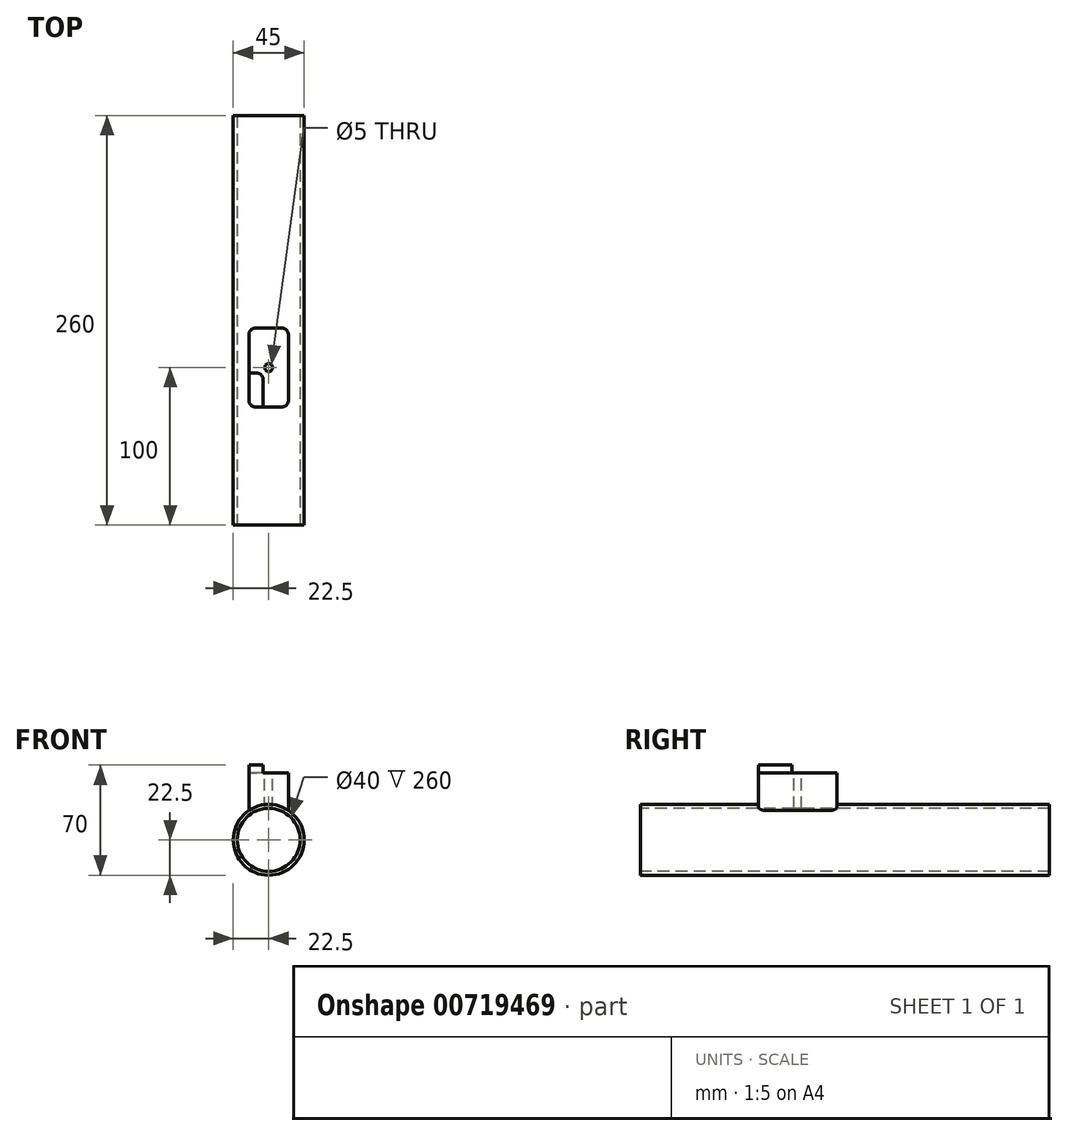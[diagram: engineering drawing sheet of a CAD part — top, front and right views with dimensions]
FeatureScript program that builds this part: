
annotation { "Feature Type Name" : "Feature", "Feature Type Description" : "" }
export const myFeature = defineFeature(function(context is Context, id is Id, definition is map)
    precondition{}
    {
        {
            var Q0;
            Q0=qCreatedBy(makeId("Right.planeOp"),FACE);
            var sketch = newSketch(context, id + "F0", { "sketchPlane" : qUnion([Q0])});
            skLineSegment(sketch, "E0", {"start": v(-15.87, 0) * mm, "end": v(20, 0) * mm, "construction": true});
            skLineSegment(sketch, "E1", {"start": v(-100, 22.5) * mm, "end": v(0, 22.5) * mm});
            skLineSegment(sketch, "E2", {"start": v(-100, 22.5) * mm, "end": v(-100, 20) * mm});
            skLineSegment(sketch, "E3", {"start": v(-100, 20) * mm, "end": v(0, 20) * mm});
            skLineSegment(sketch, "E4.MirrorCS", {"start": v(100, 20) * mm, "end": v(0, 20) * mm});
            skLineSegment(sketch, "E5.MirrorCS", {"start": v(100, 22.5) * mm, "end": v(0, 22.5) * mm});
            skLineSegment(sketch, "E6", {"start": v(-25, 22.5) * mm, "end": v(-25, 42.5) * mm});
            skLineSegment(sketch, "E7", {"start": v(-25, 42.5) * mm, "end": v(0, 42.5) * mm});
            skLineSegment(sketch, "E8", {"start": v(0, 42.5) * mm, "end": v(25, 42.5) * mm});
            skLineSegment(sketch, "E9", {"start": v(25, 42.5) * mm, "end": v(25, 22.5) * mm});
            skLineSegment(sketch, "E10", {"start": v(100, 22.5) * mm, "end": v(160, 22.5) * mm});
            skLineSegment(sketch, "E11", {"start": v(100, 20) * mm, "end": v(160, 20) * mm});
            skLineSegment(sketch, "E12", {"start": v(160, 20) * mm, "end": v(160, 22.5) * mm});
            skSolve(sketch);
        }
        {
            var Q0;
            {var subQ0=sQuery(id+"F0.wireOp",EDGE,"E2");Q0=makeQuery(id+"F0.imprint","IMPRINT",FACE,{"disambiguationData":[TD([[makeQuery(id+"F0.imprint","IMPRINT",EDGE,{"derivedFrom":subQ0}),1.0]])]});}
            var Q1;
            Q1=sQuery(id+"F0.wireOp",EDGE,"E0");
            revolve(context, id + "F1", {"surfaceOperationType" : NewSurfaceOperationType.NEW, "entities" : qUnion([Q0]), "axis" : qUnion([Q1]), "revolveType" : RevolveType.FULL});
        }
        {
            var Q0;
            {var subQ0=sQuery(id+"F0.wireOp",EDGE,"E6");Q0=makeQuery(id+"F0.imprint","IMPRINT",FACE,{"disambiguationData":[TD([[makeQuery(id+"F0.imprint","IMPRINT",EDGE,{"derivedFrom":subQ0}),-1.0]])]});}
            extrude(context, id + "F2", {"entities" : qUnion([Q0]), "operationType" : NewBodyOperationType.ADD, "endBound" : BoundingType.SYMMETRIC, "depth" : 25 * mm, "offsetDistance" : 25 * mm});
        }
        {
            var Q0;
            Q0=makeQuery(id+"F2.opExtrude","SWEPT_FACE",FACE,{"disambiguationData":[OSD([sQuery(id+"F0.wireOp",EDGE,"E9")])]});
            var sketch = newSketch(context, id + "F3", { "sketchPlane" : qUnion([Q0])});
            skLineSegment(sketch, "E13", {"start": v(-12.5, 22.5) * mm, "end": v(-12.5, 18.66) * mm});
            skLineSegment(sketch, "E14", {"start": v(-12.5, 18.66) * mm, "end": v(0, 22.5) * mm});
            skLineSegment(sketch, "E15", {"start": v(0, 22.5) * mm, "end": v(-12.5, 22.5) * mm});
            skLineSegment(sketch, "E16.MirrorCS", {"start": v(12.5, 18.66) * mm, "end": v(0, 22.5) * mm});
            skLineSegment(sketch, "E17.MirrorCS", {"start": v(0, 22.5) * mm, "end": v(12.5, 22.5) * mm});
            skLineSegment(sketch, "E18.MirrorCS", {"start": v(12.5, 22.5) * mm, "end": v(12.5, 18.66) * mm});
            skSolve(sketch);
        }
        {
            var Q0;
            Q0=makeQuery(id+"F3.imprint","IMPRINT",FACE,{"disambiguationData":[TD([[makeQuery(id+"F3.imprint","IMPRINT",EDGE,{"derivedFrom":sQuery(id+"F3.wireOp",EDGE,"E13")}),1.0]])]});
            var Q1;
            Q1=makeQuery(id+"F3.imprint","IMPRINT",FACE,{"disambiguationData":[TD([[makeQuery(id+"F3.imprint","IMPRINT",EDGE,{"derivedFrom":sQuery(id+"F3.wireOp",EDGE,"E16.MirrorCS")}),-1.0]])]});
            var Q2;
            Q2 = qSketchRegion(id + "F5", true);
            var Q3;
            Q3=sQuery(id+"F3.wireOp",EDGE,"E16.MirrorCS");
            var Q4;
            Q4=sQuery(id+"F3.wireOp",EDGE,"E15");
            var Q5;
            Q5=sQuery(id+"F3.wireOp",EDGE,"E13");
            var Q6;
            Q6=sQuery(id+"F3.wireOp",EDGE,"E18.MirrorCS");
            var Q7;
            Q7=sQuery(id+"F3.wireOp",EDGE,"E17.MirrorCS");
            var Q8;
            Q8=sQuery(id+"F3.wireOp",EDGE,"E14");
            extrude(context, id + "F4", {"entities" : qUnion([Q0, Q1, Q2]), "operationType" : NewBodyOperationType.ADD, "surfaceEntities" : qUnion([Q3, Q4, Q5, Q6, Q7, Q8]), "oppositeDirection" : true, "depth" : 50 * mm, "offsetDistance" : 25 * mm});
        }
        {
            var Q0;
            Q0=makeQuery(id+"F2.opExtrude","SWEPT_FACE",FACE,{"disambiguationData":[OSD([sQuery(id+"F0.wireOp",EDGE,"E7"),sQuery(id+"F0.wireOp",EDGE,"E8")])]});
            var sketch = newSketch(context, id + "F5", { "sketchPlane" : qUnion([Q0])});
            skLineSegment(sketch, "E19", {"start": v(12.5, 0) * mm, "end": v(-12.5, 0) * mm, "construction": true});
            skPoint(sketch, "E20", {"position": v(0, 0) * mm});
            skSolve(sketch);
        }
        {
            var Q0;
            Q0=sQuery(id+"F5.wireOp",VERTEX,"E20");
            var Q1;
            Q1=makeQuery(id+"F1.opRevolve","SWEPT_BODY",BODY,{"disambiguationData":[OSD([sQuery(id+"F0.wireOp",EDGE,"E1"),sQuery(id+"F0.wireOp",EDGE,"E2"),sQuery(id+"F0.wireOp",EDGE,"E3"),sQuery(id+"F0.wireOp",EDGE,"7791b68a-7713-4b06-8dcf-0c6fe91cb3a21.MirrorCS"),sQuery(id+"F0.wireOp",EDGE,"E4.MirrorCS"),sQuery(id+"F0.wireOp",EDGE,"E5.MirrorCS")])]});
            hole(context, id + "F6", {"style" : HoleStyle.SIMPLE, "endStyle" : HoleEndStyle.BLIND, "holeDiameter" : 5 * mm, "majorDiameter" : 5 * mm, "holeDepth" : 50 * mm, "isTappedThrough" : true, "tappedDepth" : 12 * mm, "tapClearance" : 3, "startFromSketch" : true, "locations" : qUnion([Q0]), "scope" : qUnion([Q1])});
        }
        {
            var Q0;
            Q0=makeQuery(id+"F2.opExtrude","SWEPT_FACE",FACE,{"disambiguationData":[OSD([sQuery(id+"F0.wireOp",EDGE,"E7"),sQuery(id+"F0.wireOp",EDGE,"E8")])]});
            var sketch = newSketch(context, id + "F7", { "sketchPlane" : qUnion([Q0])});
            skLineSegment(sketch, "E21", {"start": v(0, 0) * mm, "end": v(0, -3.63) * mm, "construction": true});
            skLineSegment(sketch, "E22", {"start": v(0, -3.63) * mm, "end": v(0, 0) * mm, "construction": true});
            skLineSegment(sketch, "E23", {"start": v(-3.63, 0) * mm, "end": v(0, 0) * mm, "construction": true});
            skLineSegment(sketch, "E24", {"start": v(0, -3.63) * mm, "end": v(-12.5, -3.63) * mm, "construction": true});
            skLineSegment(sketch, "E25", {"start": v(-3.62, 0) * mm, "end": v(-3.62, -25) * mm, "construction": true});
            skLineSegment(sketch, "E26.bottom", {"start": v(-12.5, -3.63) * mm, "end": v(-3.62, -3.63) * mm});
            skLineSegment(sketch, "E26.top", {"start": v(-12.5, -25) * mm, "end": v(-3.62, -25) * mm});
            skLineSegment(sketch, "E26.left", {"start": v(-12.5, -3.63) * mm, "end": v(-12.5, -25) * mm});
            skLineSegment(sketch, "E26.right", {"start": v(-3.62, -3.63) * mm, "end": v(-3.62, -25) * mm});
            skSolve(sketch);
        }
        {
            var Q0;
            Q0 = qSketchRegion(id + "F7", true);
            extrude(context, id + "F8", {"entities" : qUnion([Q0]), "operationType" : NewBodyOperationType.ADD, "depth" : 5 * mm, "offsetDistance" : 25 * mm});
        }
        {
            var Q0;
            Q0=makeQuery(id+"F8.opExtrude","SWEPT_EDGE",EDGE,{"disambiguationData":[OSD([sQuery(id+"F7.wireOp",EDGE,"E26.bottom"),sQuery(id+"F7.wireOp",EDGE,"E26.right")])]});
            fillet(context, id + "F9", {"entities" : qUnion([Q0]), "radius" : 3.62 * mm, "tangentPropagation" : true, "allowEdgeOverflow" : false});
        }
        {
            var Q0;
            Q0=makeQuery(id+"F4.boolean.opBoolean","MERGE",EDGE,{"derivedFrom":[makeQuery(id+"F2.opExtrude","CAP_EDGE",EDGE,{"disambiguationData":[OSD([sQuery(id+"F0.wireOp",EDGE,"E9")])],"isStart":false}),makeQuery(id+"F4.opExtrude","CAP_EDGE",EDGE,{"disambiguationData":[OSD([sQuery(id+"F3.wireOp",EDGE,"E13")])],"isStart":true})]});
            var Q1;
            Q1=makeQuery(id+"F4.boolean.opBoolean","MERGE",EDGE,{"derivedFrom":[makeQuery(id+"F2.opExtrude","CAP_EDGE",EDGE,{"disambiguationData":[OSD([sQuery(id+"F0.wireOp",EDGE,"E6")])],"isStart":false}),makeQuery(id+"F4.opExtrude","CAP_EDGE",EDGE,{"disambiguationData":[OSD([sQuery(id+"F3.wireOp",EDGE,"E13")])],"isStart":false})]});
            var Q2;
            Q2=makeQuery(id+"F4.boolean.opBoolean","MERGE",EDGE,{"derivedFrom":[makeQuery(id+"F2.opExtrude","CAP_EDGE",EDGE,{"disambiguationData":[OSD([sQuery(id+"F0.wireOp",EDGE,"E9")])],"isStart":true}),makeQuery(id+"F4.opExtrude","CAP_EDGE",EDGE,{"disambiguationData":[OSD([sQuery(id+"F3.wireOp",EDGE,"E18.MirrorCS")])],"isStart":true})]});
            var Q3;
            Q3=makeQuery(id+"F8.boolean.opBoolean","MERGE",EDGE,{"derivedFrom":[makeQuery(id+"F4.boolean.opBoolean","MERGE",EDGE,{"derivedFrom":[makeQuery(id+"F2.opExtrude","CAP_EDGE",EDGE,{"disambiguationData":[OSD([sQuery(id+"F0.wireOp",EDGE,"E6")])],"isStart":true}),makeQuery(id+"F4.opExtrude","CAP_EDGE",EDGE,{"disambiguationData":[OSD([sQuery(id+"F3.wireOp",EDGE,"E18.MirrorCS")])],"isStart":false})]}),makeQuery(id+"F8.opExtrude","SWEPT_EDGE",EDGE,{"disambiguationData":[OSD([sQuery(id+"F7.wireOp",EDGE,"E26.top"),sQuery(id+"F7.wireOp",EDGE,"E26.left")])]})]});
            fillet(context, id + "F10", {"entities" : qUnion([Q0, Q1, Q2, Q3]), "radius" : 4 * mm, "tangentPropagation" : true, "allowEdgeOverflow" : false});
        }
    });
